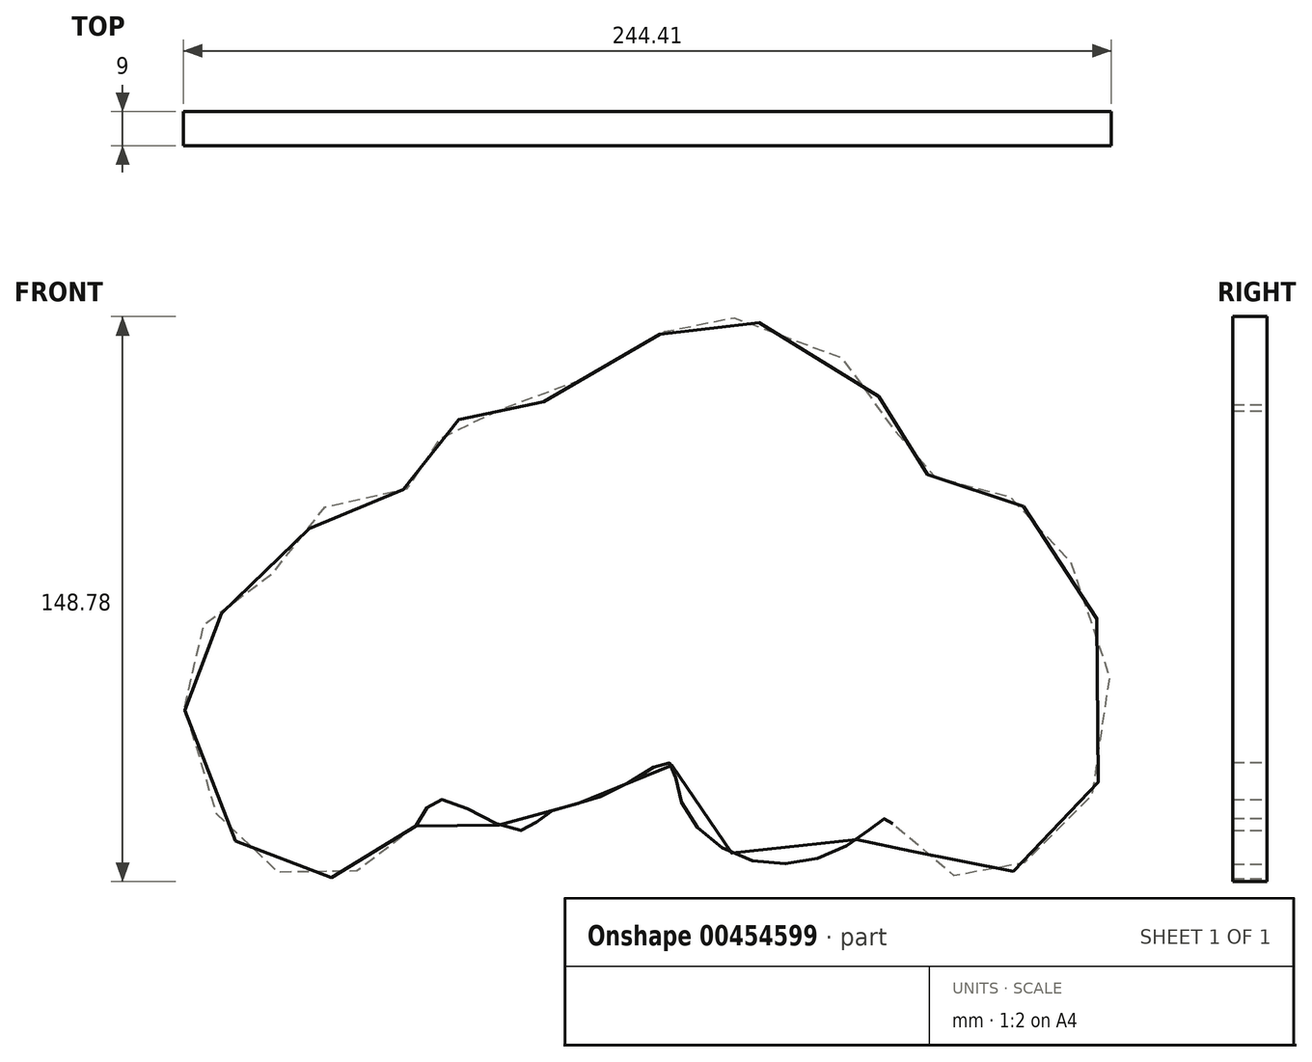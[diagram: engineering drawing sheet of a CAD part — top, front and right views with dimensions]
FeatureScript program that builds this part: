
annotation { "Feature Type Name" : "Feature", "Feature Type Description" : "" }
export const myFeature = defineFeature(function(context is Context, id is Id, definition is map)
    precondition{}
    {
        {
            var Q0;
            Q0=qCreatedBy(makeId("Front.planeOp"),FACE);
            var sketch = newSketch(context, id + "F0", { "sketchPlane" : qUnion([Q0])});
            skFitSpline(sketch, "E0", {"points": [v(-184.12, 104.68) * mm, v(-195.49, 94.53) * mm, v(-213.36, 90.87) * mm, v(-229.2, 98.18) * mm, v(-242.6, 122.96) * mm, v(-243.41, 153.42) * mm, v(-232.45, 162.35) * mm, v(-213.77, 180.63) * mm, v(-204.02, 191.2) * mm, v(-183.71, 194.44) * mm, v(-180.87, 201.75) * mm, v(-165.84, 215.56) * mm, v(-158.53, 213.93) * mm, v(-132.13, 227.34) * mm, v(-115.48, 236.27) * mm, v(-101.67, 238.7) * mm, v(-68.37, 225.3) * mm, v(-58.21, 208.65) * mm, v(-51.3, 198.1) * mm, v(-35.06, 194.44) * mm, v(-20.85, 185.91) * mm, v(-4.6, 158.7) * mm, v(-4.6, 115.65) * mm, v(-22.88, 95.75) * mm, v(-35.06, 90.06) * mm, v(-55.78, 100.21) * mm, v(-59.84, 106.71) * mm, v(-68.77, 100.62) * mm, v(-94.77, 95.34) * mm, v(-114.26, 111.18) * mm, v(-117.51, 121.33) * mm, v(-133.35, 113.21) * mm, v(-149.6, 107.93) * mm, v(-157.31, 103.46) * mm, v(-177.62, 111.59) * mm, v(-184.12, 104.68) * mm]});
            skSolve(sketch);
        }
        {
            var Q0;
            Q0 = qSketchRegion(id + "F0", true);
            extrude(context, id + "F1", {"entities" : qUnion([Q0]), "depth" : 9 * mm});
        }
    });
